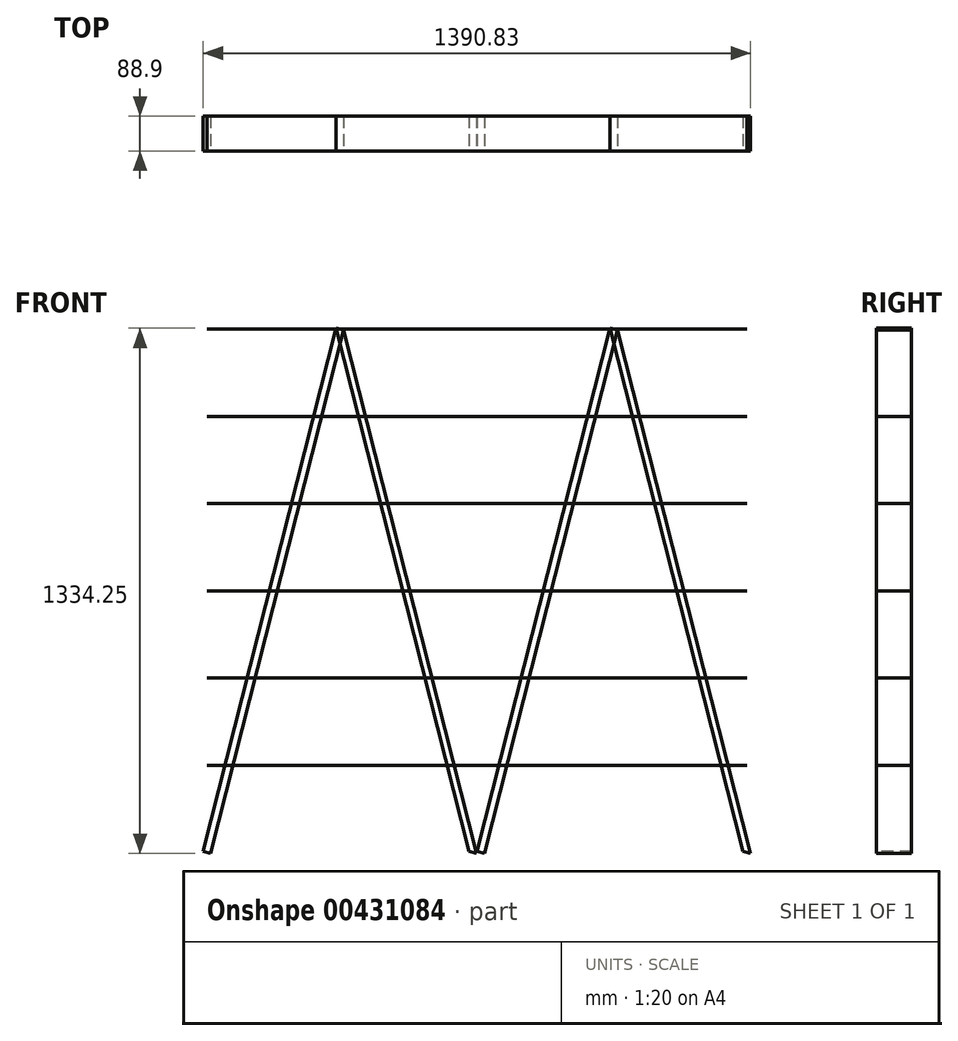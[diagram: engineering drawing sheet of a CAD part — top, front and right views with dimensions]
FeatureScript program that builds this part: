
annotation { "Feature Type Name" : "Feature", "Feature Type Description" : "" }
export const myFeature = defineFeature(function(context is Context, id is Id, definition is map)
    precondition{}
    {
        {
            var Q0;
            Q0=qCreatedBy(makeId("Front.planeOp"),FACE);
            var sketch = newSketch(context, id + "F0", { "sketchPlane" : qUnion([Q0])});
            skLineSegment(sketch, "E0", {"start": v(-53, 736.07) * mm, "end": v(-390.73, -593.3) * mm});
            skLineSegment(sketch, "E1", {"start": v(-53, 736.07) * mm, "end": v(284.75, -593.3) * mm});
            skLineSegment(sketch, "E2", {"start": v(284.75, -593.3) * mm, "end": v(305.39, -593.3) * mm});
            skLineSegment(sketch, "E3", {"start": v(305.39, -593.3) * mm, "end": v(643.13, 736.07) * mm});
            skLineSegment(sketch, "E4", {"start": v(643.13, 736.07) * mm, "end": v(980.87, -593.3) * mm});
            skLineSegment(sketch, "E5", {"start": v(-390.73, -593.3) * mm, "end": v(980.87, -593.3) * mm, "construction": true});
            skLineSegment(sketch, "E6", {"start": v(-390.73, -593.3) * mm, "end": v(-390.73, -645.75) * mm, "construction": true});
            skLineSegment(sketch, "E7", {"start": v(284.75, -593.3) * mm, "end": v(284.75, -645.75) * mm, "construction": true});
            skLineSegment(sketch, "E8", {"start": v(305.39, -593.3) * mm, "end": v(305.39, -645.75) * mm, "construction": true});
            skLineSegment(sketch, "E9", {"start": v(980.87, -593.3) * mm, "end": v(980.87, -645.75) * mm, "construction": true});
            skLineSegment(sketch, "E10", {"start": v(-390.73, -645.75) * mm, "end": v(284.75, -645.75) * mm, "construction": true});
            skLineSegment(sketch, "E11", {"start": v(305.39, -645.75) * mm, "end": v(980.87, -645.75) * mm, "construction": true});
            skLineSegment(sketch, "E12", {"start": v(980.87, 736.07) * mm, "end": v(-390.73, 736.07) * mm});
            skLineSegment(sketch, "E13", {"start": v(980.87, -593.3) * mm, "end": v(980.87, 1010.18) * mm, "construction": true});
            skLineSegment(sketch, "E14", {"start": v(980.87, 514.5) * mm, "end": v(-390.73, 514.5) * mm});
            skLineSegment(sketch, "E15", {"start": v(980.87, 292.94) * mm, "end": v(-390.73, 292.94) * mm});
            skLineSegment(sketch, "E16", {"start": v(980.87, 71.38) * mm, "end": v(-390.73, 71.38) * mm});
            skLineSegment(sketch, "E17", {"start": v(980.87, -150.18) * mm, "end": v(-390.73, -150.18) * mm});
            skLineSegment(sketch, "E18", {"start": v(980.87, -371.74) * mm, "end": v(-390.73, -371.74) * mm});
            skLineSegment(sketch, "E19", {"start": v(643.13, 736.07) * mm, "end": v(643.13, 514.5) * mm, "construction": true});
            skLineSegment(sketch, "E20", {"start": v(643.13, 514.5) * mm, "end": v(643.13, 292.94) * mm, "construction": true});
            skLineSegment(sketch, "E21", {"start": v(643.13, 292.94) * mm, "end": v(643.13, 71.38) * mm, "construction": true});
            skLineSegment(sketch, "E22", {"start": v(643.13, 71.38) * mm, "end": v(643.13, -150.18) * mm, "construction": true});
            skLineSegment(sketch, "E23", {"start": v(643.13, -150.18) * mm, "end": v(643.13, -371.74) * mm, "construction": true});
            skLineSegment(sketch, "E24", {"start": v(643.13, -371.74) * mm, "end": v(643.13, -593.3) * mm, "construction": true});
            skSolve(sketch);
        }
        {
            var Q0;
            Q0=sQuery(id+"F0.wireOp",EDGE,"E12");
            var Q1;
            Q1=sQuery(id+"F0.wireOp",EDGE,"E14");
            var Q2;
            Q2=sQuery(id+"F0.wireOp",EDGE,"E15");
            var Q3;
            Q3=sQuery(id+"F0.wireOp",EDGE,"E16");
            var Q4;
            Q4=sQuery(id+"F0.wireOp",EDGE,"E17");
            var Q5;
            Q5=sQuery(id+"F0.wireOp",EDGE,"E18");
            extrude(context, id + "F1", {"bodyType" : ToolBodyType.SURFACE, "surfaceEntities" : qUnion([Q0, Q1, Q2, Q3, Q4, Q5]), "depth" : 88.9 * mm});
        }
        {
            var Q0;
            Q0=makeQuery(id+"F1.opExtrude","SWEPT_FACE",FACE,{"disambiguationData":[OSD([sQuery(id+"F0.wireOp",EDGE,"E18")])]});
            var Q1;
            Q1=makeQuery(id+"F1.opExtrude","SWEPT_FACE",FACE,{"disambiguationData":[OSD([sQuery(id+"F0.wireOp",EDGE,"E17")])]});
            var Q2;
            Q2=makeQuery(id+"F1.opExtrude","SWEPT_FACE",FACE,{"disambiguationData":[OSD([sQuery(id+"F0.wireOp",EDGE,"E16")])]});
            var Q3;
            Q3=makeQuery(id+"F1.opExtrude","SWEPT_FACE",FACE,{"disambiguationData":[OSD([sQuery(id+"F0.wireOp",EDGE,"E15")])]});
            var Q4;
            Q4=makeQuery(id+"F1.opExtrude","SWEPT_FACE",FACE,{"disambiguationData":[OSD([sQuery(id+"F0.wireOp",EDGE,"E14")])]});
            var Q5;
            Q5=makeQuery(id+"F1.opExtrude","SWEPT_FACE",FACE,{"disambiguationData":[OSD([sQuery(id+"F0.wireOp",EDGE,"E12")])]});
            extrude(context, id + "F2", {"entities" : qUnion([Q0, Q1, Q2, Q3, Q4, Q5]), "depth" : 23 / 1625.6 * mm, "hasSecondDirection" : true, "secondDirectionOppositeDirection" : true, "secondDirectionDepth" : 23 / 1625.6 * mm});
        }
        {
            var Q0;
            Q0=sQuery(id+"F0.wireOp",EDGE,"E0");
            var Q1;
            Q1=sQuery(id+"F0.wireOp",EDGE,"E1");
            var Q2;
            Q2=sQuery(id+"F0.wireOp",EDGE,"E3");
            var Q3;
            Q3=sQuery(id+"F0.wireOp",EDGE,"E4");
            extrude(context, id + "F3", {"bodyType" : ToolBodyType.SURFACE, "surfaceEntities" : qUnion([Q0, Q1, Q2, Q3]), "depth" : 88.9 * mm});
        }
        {
            var Q0;
            Q0=makeQuery(id+"F3.opExtrude","SWEPT_FACE",FACE,{"disambiguationData":[OSD([sQuery(id+"F0.wireOp",EDGE,"E0")])]});
            var Q1;
            Q1=makeQuery(id+"F3.opExtrude","SWEPT_FACE",FACE,{"disambiguationData":[OSD([sQuery(id+"F0.wireOp",EDGE,"E1")])]});
            var Q2;
            Q2=makeQuery(id+"F3.opExtrude","SWEPT_FACE",FACE,{"disambiguationData":[OSD([sQuery(id+"F0.wireOp",EDGE,"E3")])]});
            var Q3;
            Q3=makeQuery(id+"F3.opExtrude","SWEPT_FACE",FACE,{"disambiguationData":[OSD([sQuery(id+"F0.wireOp",EDGE,"E4")])]});
            extrude(context, id + "F4", {"entities" : qUnion([Q0, Q1, Q2, Q3]), "depth" : 9.92 * mm, "hasSecondDirection" : true, "secondDirectionOppositeDirection" : true, "secondDirectionDepth" : 9.92 * mm});
        }
    });
